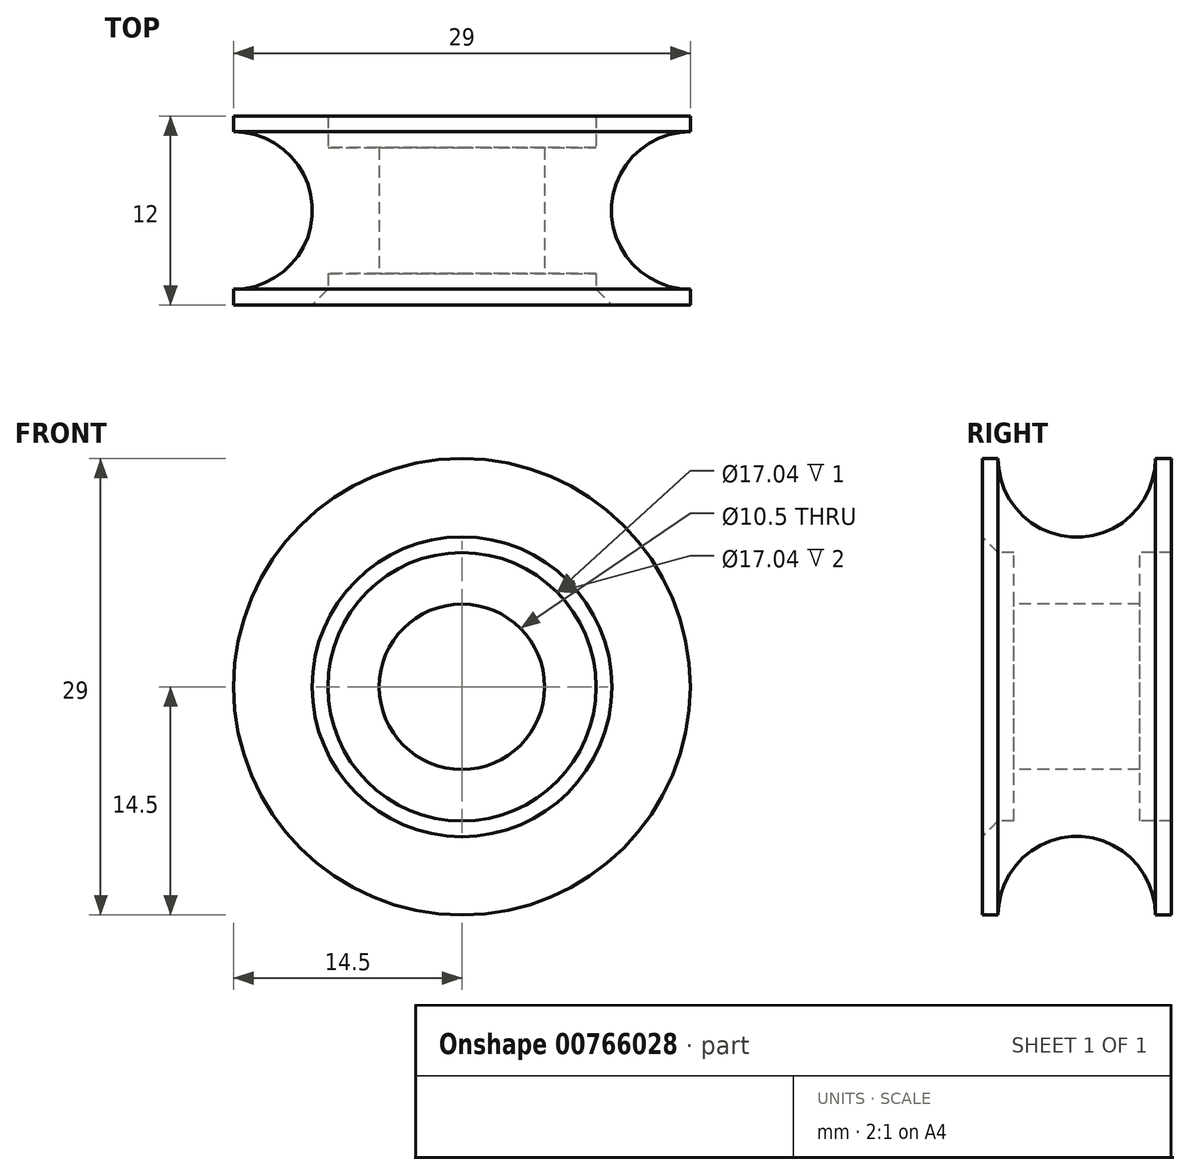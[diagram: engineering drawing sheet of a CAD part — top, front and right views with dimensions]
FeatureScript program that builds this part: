
annotation { "Feature Type Name" : "Feature", "Feature Type Description" : "" }
export const myFeature = defineFeature(function(context is Context, id is Id, definition is map)
    precondition{}
    {
        {
            var Q0;
            Q0=qCreatedBy(makeId("Front.planeOp"),FACE);
            var sketch = newSketch(context, id + "F0", { "sketchPlane" : qUnion([Q0])});
            skCircle(sketch, "E0", {"center": v(0, 0) * mm, "radius": 14.5 * mm});
            skSolve(sketch);
        }
        {
            var Q0;
            Q0=makeQuery(id+"F0.imprint","IMPRINT",FACE,{"disambiguationData":[TD([[makeQuery(id+"F0.imprint","IMPRINT",EDGE,{"derivedFrom":sQuery(id+"F0.wireOp",EDGE,"E0")}),1.0]])]});
            extrude(context, id + "F1", {"entities" : qUnion([Q0]), "depth" : 12 * mm, "offsetDistance" : 25 * mm});
        }
        {
            var Q0;
            Q0=qCreatedBy(makeId("Top.planeOp"),FACE);
            var sketch = newSketch(context, id + "F2", { "sketchPlane" : qUnion([Q0])});
            skLineSegment(sketch, "E1", {"start": v(-14.5, -12) * mm, "end": v(-14.5, 0) * mm, "construction": true});
            skLineSegment(sketch, "E2", {"start": v(14.5, 0) * mm, "end": v(14.5, -12) * mm, "construction": true});
            skCircle(sketch, "E3", {"center": v(14.5, -6) * mm, "radius": 5 * mm});
            skLineSegment(sketch, "E4", {"start": v(0, 0) * mm, "end": v(0, -16.56) * mm, "construction": true});
            skLineSegment(sketch, "E5.bottom", {"start": v(0, -2) * mm, "end": v(5.25, -2) * mm});
            skLineSegment(sketch, "E5.top", {"start": v(0, -10) * mm, "end": v(5.25, -10) * mm});
            skLineSegment(sketch, "E5.left", {"start": v(0, -2) * mm, "end": v(0, -10) * mm});
            skLineSegment(sketch, "E5.right", {"start": v(5.25, -2) * mm, "end": v(5.25, -10) * mm});
            skPoint(sketch, "E6", {"position": v(5.25, -6) * mm});
            skPoint(sketch, "E7", {"position": v(-14.5, -6) * mm});
            skLineSegment(sketch, "E8.bottom", {"start": v(0, -2) * mm, "end": v(8.52, -2) * mm});
            skLineSegment(sketch, "E8.top", {"start": v(0, 0) * mm, "end": v(8.52, 0) * mm});
            skLineSegment(sketch, "E8.left", {"start": v(0, -2) * mm, "end": v(0, 0) * mm});
            skLineSegment(sketch, "E8.right", {"start": v(8.52, -2) * mm, "end": v(8.52, 0) * mm});
            skLineSegment(sketch, "E9.bottom", {"start": v(0, -10) * mm, "end": v(8.52, -10) * mm});
            skLineSegment(sketch, "E9.top", {"start": v(0, -12.97) * mm, "end": v(8.52, -12.97) * mm});
            skLineSegment(sketch, "E9.left", {"start": v(0, -10) * mm, "end": v(0, -12.97) * mm});
            skLineSegment(sketch, "E9.right", {"start": v(8.52, -10) * mm, "end": v(8.52, -12.97) * mm});
            skSolve(sketch);
        }
        {
            var Q0;
            {var subQ0=sQuery(id+"F2.wireOp",EDGE,"E5.left");Q0=makeQuery(id+"F2.imprint","IMPRINT",FACE,{"disambiguationData":[TD([[makeQuery(id+"F2.imprint","IMPRINT",EDGE,{"derivedFrom":subQ0}),1.0]])]});}
            var Q1;
            Q1=makeQuery(id+"F2.imprint","IMPRINT",FACE,{"disambiguationData":[TD([[makeQuery(id+"F2.imprint","IMPRINT",EDGE,{"derivedFrom":sQuery(id+"F2.wireOp",EDGE,"E9.top")}),1.0]])]});
            var Q2;
            Q2=makeQuery(id+"F2.imprint","IMPRINT",FACE,{"disambiguationData":[TD([[makeQuery(id+"F2.imprint","IMPRINT",EDGE,{"derivedFrom":sQuery(id+"F2.wireOp",EDGE,"E8.top")}),-1.0]])]});
            var Q3;
            Q3=makeQuery(id+"F2.imprint","IMPRINT",FACE,{"disambiguationData":[TD([[makeQuery(id+"F2.imprint","IMPRINT",EDGE,{"derivedFrom":sQuery(id+"F2.wireOp",EDGE,"E3")}),1.0]])]});
            var Q4;
            Q4=sQuery(id+"F2.wireOp",EDGE,"E4");
            revolve(context, id + "F3", {"operationType" : NewBodyOperationType.REMOVE, "surfaceOperationType" : NewSurfaceOperationType.NEW, "entities" : qUnion([Q0, Q1, Q2, Q3]), "axis" : qUnion([Q4]), "revolveType" : RevolveType.FULL, "oppositeDirection" : true});
        }
        {
            var Q0;
            Q0=makeQuery(id+"F3.boolean.opBoolean","COPY",EDGE,{"derivedFrom":makeQuery(id+"F3.opRevolve","SWEPT_EDGE",EDGE,{"disambiguationData":[OSD([sQuery(id+"F2.wireOp",EDGE,"E8.top"),sQuery(id+"F2.wireOp",EDGE,"E8.right")])]})});
            var Q1;
            Q1=makeQuery(id+"F3.boolean.opBoolean","INTERSECT",EDGE,{"derivedFrom":[makeQuery(id+"F1.opExtrude","CAP_FACE",FACE,{"disambiguationData":[OSD([sQuery(id+"F0.wireOp",EDGE,"E0")])],"isStart":false}),makeQuery(id+"F3.opRevolve","SWEPT_FACE",FACE,{"disambiguationData":[OSD([sQuery(id+"F2.wireOp",EDGE,"E9.right")])]})]});
            chamfer(context, id + "F4", {"entities" : qUnion([Q0, Q1]), "width" : 1 * mm, "tangentPropagation" : true});
        }
    });
